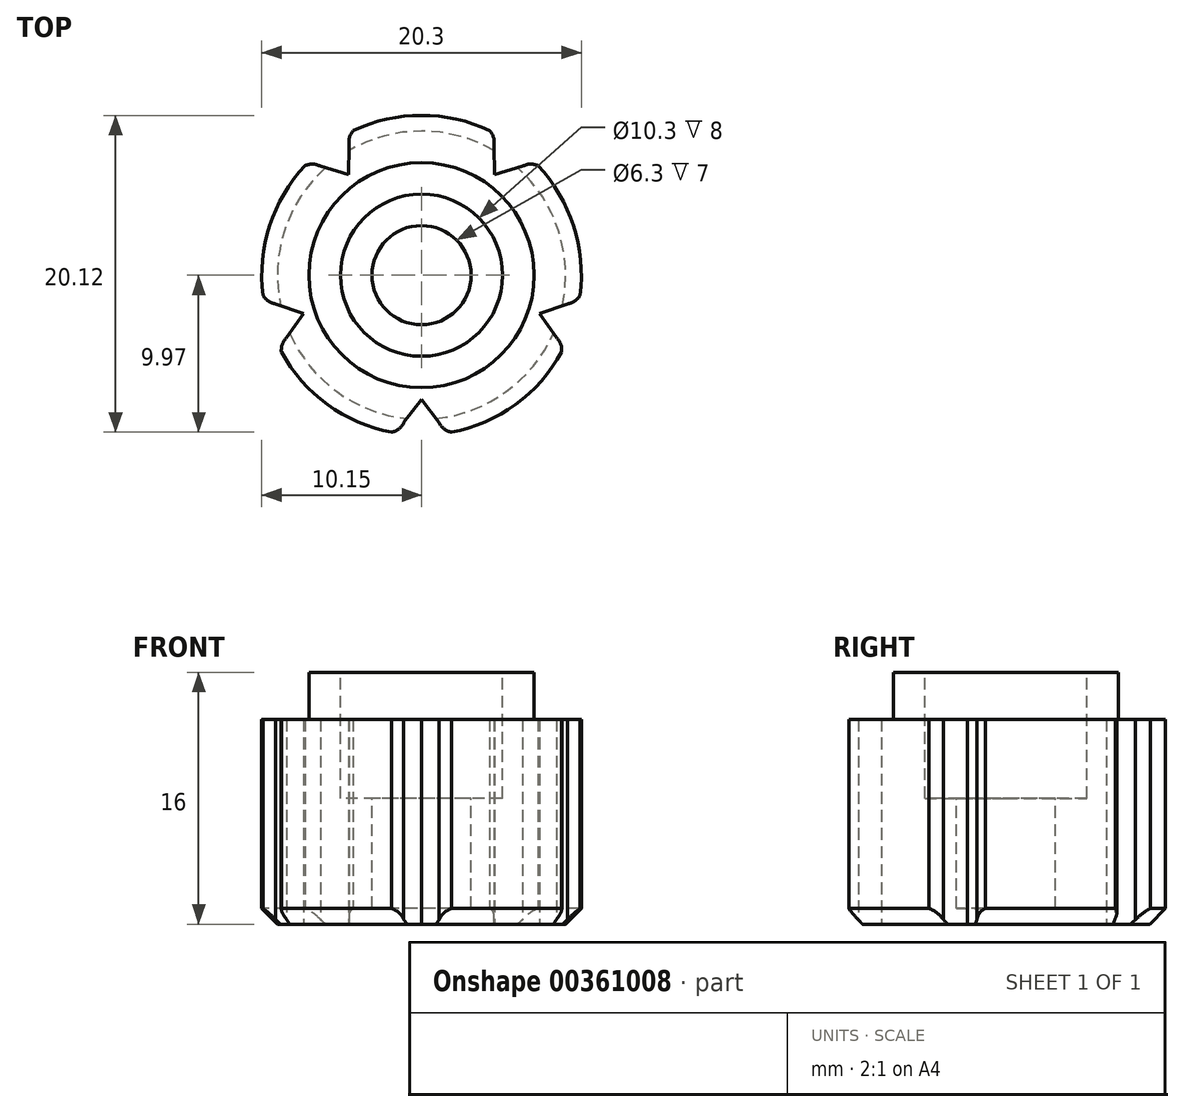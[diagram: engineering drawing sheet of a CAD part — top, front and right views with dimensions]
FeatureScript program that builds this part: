
annotation { "Feature Type Name" : "Feature", "Feature Type Description" : "" }
export const myFeature = defineFeature(function(context is Context, id is Id, definition is map)
    precondition{}
    {
        {
            var Q0;
            Q0=qCreatedBy(makeId("Front.planeOp"),FACE);
            var sketch = newSketch(context, id + "F0", { "sketchPlane" : qUnion([Q0])});
            skLineSegment(sketch, "E0", {"start": v(-10.15, 0) * mm, "end": v(-10.15, 13) * mm});
            skLineSegment(sketch, "E1", {"start": v(-10.15, 13) * mm, "end": v(-7.15, 13) * mm});
            skLineSegment(sketch, "E2", {"start": v(-7.15, 13) * mm, "end": v(-7.15, 16) * mm});
            skLineSegment(sketch, "E3", {"start": v(0, 0) * mm, "end": v(-10.15, 0) * mm});
            skLineSegment(sketch, "E4", {"start": v(0, 1) * mm, "end": v(-3.15, 1) * mm});
            skLineSegment(sketch, "E5", {"start": v(-3.15, 1) * mm, "end": v(-3.15, 8) * mm});
            skLineSegment(sketch, "E6", {"start": v(-3.15, 8) * mm, "end": v(-5.15, 8) * mm});
            skLineSegment(sketch, "E7", {"start": v(-5.15, 8) * mm, "end": v(-5.15, 16) * mm});
            skLineSegment(sketch, "E8", {"start": v(0, 0) * mm, "end": v(0, -17.26) * mm, "construction": true});
            skLineSegment(sketch, "E9", {"start": v(-7.15, 16) * mm, "end": v(-5.15, 16) * mm});
            skLineSegment(sketch, "E10", {"start": v(0, 1) * mm, "end": v(0, 0) * mm});
            skSolve(sketch);
        }
        {
            var Q0;
            Q0 = qSketchRegion(id + "F0", true);
            var Q1;
            Q1=sQuery(id+"F0.wireOp",EDGE,"E8");
            revolve(context, id + "F1", {"entities" : qUnion([Q0]), "axis" : qUnion([Q1]), "revolveType" : RevolveType.FULL});
        }
        {
            var Q0;
            Q0=qCreatedBy(makeId("Top.planeOp"),FACE);
            var sketch = newSketch(context, id + "F2", { "sketchPlane" : qUnion([Q0])});
            skLineSegment(sketch, "E11", {"start": v(0, -7.9) * mm, "end": v(0, -9.31) * mm, "construction": true});
            skLineSegment(sketch, "E12", {"start": v(-1.22, -9.5) * mm, "end": v(0, -7.9) * mm});
            skLineSegment(sketch, "E13", {"start": v(1.13, -9.37) * mm, "end": v(0, -7.9) * mm});
            skArc(sketch, "E14", {"start": v(1.13, -9.37) * mm, "mid": v(1.44, -9.76) * mm, "end": v(1.9, -9.97) * mm});
            skArc(sketch, "E15.MirrorCS", {"start": v(-1.13, -9.37) * mm, "mid": v(-1.44, -9.76) * mm, "end": v(-1.9, -9.97) * mm});
            skArc(sketch, "E16", {"start": v(-1.9, -9.97) * mm, "mid": v(0, -11.32) * mm, "end": v(1.9, -9.97) * mm});
            skLineSegment(sketch, "E17.1.0", {"start": v(8.66, -4.1) * mm, "end": v(7.5, -2.44) * mm});
            skLineSegment(sketch, "E17.1.1", {"start": v(9.26, -1.83) * mm, "end": v(7.5, -2.44) * mm});
            skArc(sketch, "E17.1.2", {"start": v(9.26, -1.83) * mm, "mid": v(9.73, -1.65) * mm, "end": v(10.07, -1.28) * mm});
            skArc(sketch, "E17.1.3", {"start": v(8.57, -3.97) * mm, "mid": v(8.84, -4.39) * mm, "end": v(8.9, -4.88) * mm});
            skArc(sketch, "E17.1.4", {"start": v(8.9, -4.88) * mm, "mid": v(10.77, -3.5) * mm, "end": v(10.07, -1.28) * mm});
            skLineSegment(sketch, "E17.2.0", {"start": v(6.57, 6.97) * mm, "end": v(4.64, 6.38) * mm});
            skLineSegment(sketch, "E17.2.1", {"start": v(4.6, 8.24) * mm, "end": v(4.64, 6.38) * mm});
            skArc(sketch, "E17.2.2", {"start": v(4.6, 8.24) * mm, "mid": v(4.57, 8.75) * mm, "end": v(4.33, 9.18) * mm});
            skArc(sketch, "E17.2.3", {"start": v(6.42, 6.92) * mm, "mid": v(6.9, 7.05) * mm, "end": v(7.4, 6.95) * mm});
            skArc(sketch, "E17.2.4", {"start": v(7.4, 6.95) * mm, "mid": v(6.65, 9.16) * mm, "end": v(4.33, 9.18) * mm});
            skLineSegment(sketch, "E17.3.0", {"start": v(-4.6, 8.4) * mm, "end": v(-4.64, 6.38) * mm});
            skLineSegment(sketch, "E17.3.1", {"start": v(-6.42, 6.92) * mm, "end": v(-4.64, 6.38) * mm});
            skArc(sketch, "E17.3.2", {"start": v(-6.42, 6.92) * mm, "mid": v(-6.9, 7.05) * mm, "end": v(-7.4, 6.95) * mm});
            skArc(sketch, "E17.3.3", {"start": v(-4.6, 8.24) * mm, "mid": v(-4.57, 8.75) * mm, "end": v(-4.33, 9.18) * mm});
            skArc(sketch, "E17.3.4", {"start": v(-4.33, 9.18) * mm, "mid": v(-6.65, 9.16) * mm, "end": v(-7.4, 6.95) * mm});
            skLineSegment(sketch, "E17.4.0", {"start": v(-9.41, -1.77) * mm, "end": v(-7.5, -2.44) * mm});
            skLineSegment(sketch, "E17.4.1", {"start": v(-8.57, -3.97) * mm, "end": v(-7.5, -2.44) * mm});
            skArc(sketch, "E17.4.2", {"start": v(-8.57, -3.97) * mm, "mid": v(-8.84, -4.39) * mm, "end": v(-8.9, -4.88) * mm});
            skArc(sketch, "E17.4.3", {"start": v(-9.26, -1.83) * mm, "mid": v(-9.73, -1.65) * mm, "end": v(-10.07, -1.28) * mm});
            skArc(sketch, "E17.4.4", {"start": v(-10.07, -1.28) * mm, "mid": v(-10.77, -3.5) * mm, "end": v(-8.9, -4.88) * mm});
            skPoint(sketch, "E17.center", {"position": v(0, 0) * mm});
            skSolve(sketch);
        }
        {
            var Q0;
            Q0 = qSketchRegion(id + "F2", true);
            extrude(context, id + "F3", {"entities" : qUnion([Q0]), "operationType" : NewBodyOperationType.REMOVE, "endBound" : BoundingType.THROUGH_ALL, "depth" : 5 * mm});
        }
        {
            var Q0;
            {var subQ0=sQuery(id+"F0.wireOp",EDGE,"E0");var subQ1=sQuery(id+"F0.wireOp",EDGE,"E3");Q0=makeQuery(id+"F3.boolean.opBoolean","SPLIT",EDGE,{"disambiguationData":[TD([makeQuery(id+"F3.opExtrude","SWEPT_FACE",FACE,{"disambiguationData":[OSD([sQuery(id+"F2.wireOp",EDGE,"E15.MirrorCS")])]})])],"derivedFrom":makeQuery(id+"F1.opRevolve","SWEPT_EDGE",EDGE,{"disambiguationData":[OSD([subQ0,subQ1])]})});}
            var Q1;
            {var subQ0=sQuery(id+"F0.wireOp",EDGE,"E0");var subQ1=sQuery(id+"F0.wireOp",EDGE,"E3");Q1=makeQuery(id+"F3.boolean.opBoolean","SPLIT",EDGE,{"disambiguationData":[TD([makeQuery(id+"F3.opExtrude","SWEPT_FACE",FACE,{"disambiguationData":[OSD([sQuery(id+"F2.wireOp",EDGE,"E14")])]})])],"derivedFrom":makeQuery(id+"F1.opRevolve","SWEPT_EDGE",EDGE,{"disambiguationData":[OSD([subQ0,subQ1])]})});}
            var Q2;
            {var subQ0=sQuery(id+"F0.wireOp",EDGE,"E0");var subQ1=sQuery(id+"F0.wireOp",EDGE,"E3");Q2=makeQuery(id+"F3.boolean.opBoolean","SPLIT",EDGE,{"disambiguationData":[TD([makeQuery(id+"F3.opExtrude","SWEPT_FACE",FACE,{"disambiguationData":[OSD([sQuery(id+"F2.wireOp",EDGE,"E17.1.2")])]})])],"derivedFrom":makeQuery(id+"F1.opRevolve","SWEPT_EDGE",EDGE,{"disambiguationData":[OSD([subQ0,subQ1])]})});}
            var Q3;
            {var subQ0=sQuery(id+"F0.wireOp",EDGE,"E0");var subQ1=sQuery(id+"F0.wireOp",EDGE,"E3");Q3=makeQuery(id+"F3.boolean.opBoolean","SPLIT",EDGE,{"disambiguationData":[TD([makeQuery(id+"F3.opExtrude","SWEPT_FACE",FACE,{"disambiguationData":[OSD([sQuery(id+"F2.wireOp",EDGE,"E17.2.2")])]})])],"derivedFrom":makeQuery(id+"F1.opRevolve","SWEPT_EDGE",EDGE,{"disambiguationData":[OSD([subQ0,subQ1])]})});}
            var Q4;
            {var subQ0=sQuery(id+"F0.wireOp",EDGE,"E0");var subQ1=sQuery(id+"F0.wireOp",EDGE,"E3");Q4=makeQuery(id+"F3.boolean.opBoolean","SPLIT",EDGE,{"disambiguationData":[TD([makeQuery(id+"F3.opExtrude","SWEPT_FACE",FACE,{"disambiguationData":[OSD([sQuery(id+"F2.wireOp",EDGE,"E17.3.2")])]})])],"derivedFrom":makeQuery(id+"F1.opRevolve","SWEPT_EDGE",EDGE,{"disambiguationData":[OSD([subQ0,subQ1])]})});}
            chamfer(context, id + "F4", {"entities" : qUnion([Q0, Q1, Q2, Q3, Q4]), "width" : 1 * mm, "tangentPropagation" : true});
        }
    });
